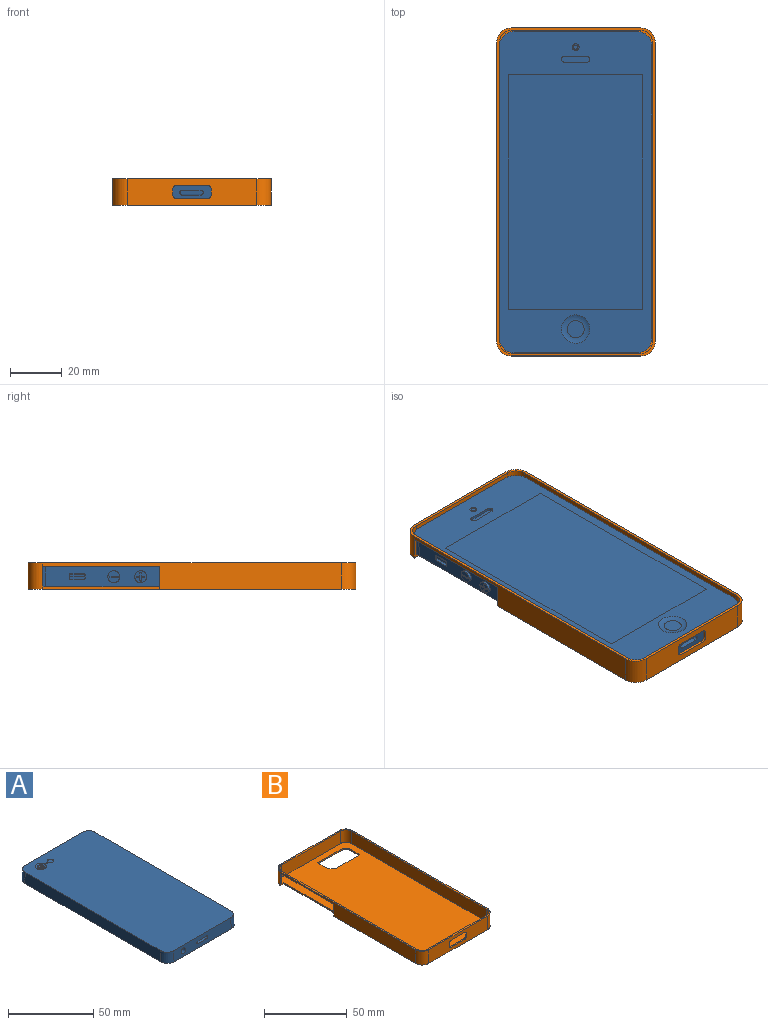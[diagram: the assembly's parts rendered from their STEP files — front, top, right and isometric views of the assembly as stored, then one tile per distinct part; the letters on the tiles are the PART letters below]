
ASSEMBLY  parts=2 mates=1
PART A: 118 faces, bbox 59.5x124.3x7.6 mm
  f0: plane 47.4x7.6mm, normal (0,1,0.05), area 338.2mm2, adj f6,f7,f9,f10,f109,f110,f111,f112
  f1: plane 6x2.52mm, normal (1,0,0.05), area 9.6mm2, adj f40,f41,f42,f43,f44,f45,f46,f47
  f2: cone r=5.6mm half-angle=3deg, axis (0,0,-1), area 64.6mm2, adj f3,f8,f9,f10
  f3: plane 47.4x7.6mm, normal (0,-1,0.05), area 334.5mm2, adj f2,f4,f9,f10,f29,f30,f31,f32
  f4: cone r=5.6mm half-angle=3deg, axis (0,0,-1), area 64.6mm2, adj f3,f5,f9,f10
  f5: plane 112.6x7.6mm, normal (1,0,0.05), area 808.8mm2, adj f4,f6,f9,f10,f40,f41,f42,f43
  f6: cone r=5.6mm half-angle=3deg, axis (0,0,-1), area 64.6mm2, adj f0,f5,f9,f10
  f7: cone r=5.6mm half-angle=3deg, axis (0,0,-1), area 64.6mm2, adj f0,f8,f9,f10
  f8: plane 112.6x7.6mm, normal (-1,0,0.05), area 856.9mm2, adj f2,f7,f9,f10
  f9: plane 123x57.8mm, normal (0,0,1), area 7041.8mm2, adj f0,f2,f3,f4,f5,f6,f7,f8
  f10: plane 123.8x58.6mm, normal (0,0,-1), area 2431.8mm2, adj f0,f2,f3,f4,f5,f6,f7,f8
  f11: plane 6.54x6.54mm, normal (0,0,-1), area 33.6mm2, adj f12
  f12: torus R=3.27mm, axis (0,0,1), area 62mm2, adj f10,f11
  f13: plane 90.39x0mm, normal (1,0,0), area 0mm2, adj f10,f17
  f14: plane 51.7x0mm, normal (0,-1,0), area 0mm2, adj f10,f17
  f15: plane 90.39x0mm, normal (-1,0,0), area 0mm2, adj f10,f17
  f16: plane 51.7x0mm, normal (0,1,0), area 0mm2, adj f10,f17
  f17: plane 90.39x51.7mm, normal (0,0,-1), area 4673.2mm2, adj f13,f14,f15,f16
  f18: cylinder r=1.1mm len=1.1mm, axis (0,0,-1), area 1.7mm2, adj f10,f19,f25,f26
  f19: plane 8.7x1mm, normal (0,1,0), area 8.7mm2, adj f10,f18,f20,f26
  f20: cylinder r=1.1mm len=1.1mm, axis (0,0,-1), area 1.7mm2, adj f10,f19,f21,f26
  f21: plane 1x0.1mm, normal (1,0,0), area 0.1mm2, adj f10,f20,f22,f26
  f22: cylinder r=1.1mm len=1.1mm, axis (0,0,-1), area 1.7mm2, adj f10,f21,f23,f26
  f23: plane 8.7x1mm, normal (0,-1,0), area 8.7mm2, adj f10,f22,f24,f26
  f24: cylinder r=1.1mm len=1.1mm, axis (0,0,-1), area 1.7mm2, adj f10,f23,f25,f26
  f25: plane 1x0.1mm, normal (-1,0,0), area 0.1mm2, adj f10,f18,f24,f26
  f26: plane 10.9x2.3mm, normal (0,0,-1), area 24mm2, adj f18,f19,f20,f21,f22,f23,f24,f25
  f27: plane 1.56x1.56mm, normal (0,0,-1), area 1.9mm2, adj f28
  f28: torus R=0.78mm, axis (0,0,1), area 3.6mm2, adj f10,f27
  f29: cylinder r=0.9mm len=5.04mm, axis (0,-1,0.05), area 7.1mm2, adj f3,f30,f36,f37
  f30: plane 7.25x4.99mm, normal (0,0.05,1), area 36.2mm2, adj f3,f29,f31,f37
  f31: cylinder r=0.9mm len=5.04mm, axis (0,-1,0.05), area 7.1mm2, adj f3,f30,f32,f37
  f32: plane 5x0.34mm, normal (-1,0,0), area 0.4mm2, adj f3,f31,f33,f37
  f33: cylinder r=0.9mm len=5.04mm, axis (0,-1,0.05), area 7.1mm2, adj f3,f32,f34,f37
  f34: plane 7.25x4.99mm, normal (0,-0.05,-1), area 36.3mm2, adj f3,f33,f35,f37
  f35: cylinder r=0.9mm len=5.04mm, axis (0,-1,0.05), area 7.1mm2, adj f3,f34,f36,f37
  f36: plane 5x0.34mm, normal (1,0,0), area 0.4mm2, adj f3,f29,f35,f37
  f37: plane 9.05x1.88mm, normal (0,-1,0.05), area 16.3mm2, adj f29,f30,f31,f32,f33,f34,f35,f36
  f38: cylinder r=1.78mm len=10.17mm, axis (0,-1,0.05), area 111.8mm2, adj f3,f39
  f39: plane 3.56x3.56mm, normal (0,-1,0.05), area 10mm2, adj f38
  f40: plane 5x1.5mm, normal (-0.05,0,1), area 7.5mm2, adj f1,f5,f41,f47
  f41: cylinder r=0.5mm len=1.52mm, axis (1,0,0.05), area 1.2mm2, adj f1,f5,f40,f42
  f42: plane 1.6x1.58mm, normal (0,-1,0), area 2.3mm2, adj f1,f5,f41,f43
  f43: cylinder r=0.5mm len=1.52mm, axis (1,0,0.05), area 1.2mm2, adj f1,f5,f42,f44
  f44: plane 5x1.5mm, normal (0.05,0,-1), area 7.5mm2, adj f1,f5,f43,f45
  f45: cylinder r=0.5mm len=1.52mm, axis (1,0,0.05), area 1.2mm2, adj f1,f5,f44,f46
  f46: plane 1.6x1.58mm, normal (0,1,0), area 2.3mm2, adj f1,f5,f45,f47
  f47: cylinder r=0.5mm len=1.52mm, axis (1,0,0.05), area 1.2mm2, adj f1,f5,f40,f46
  f48: cylinder r=2.3mm len=4.65mm, axis (-1,0,-0.05), area 14.5mm2, adj f5,f49
  f49: plane 4.6x4.59mm, normal (1,0,0.05), area 15.1mm2, adj f48,f61,f62,f63,f64,f65,f66,f67
  f50: cylinder r=2.3mm len=4.65mm, axis (-1,0,-0.05), area 14.5mm2, adj f5,f51
  f51: plane 4.6x4.59mm, normal (1,0,0.05), area 13.8mm2, adj f50,f70,f71,f72,f73,f74,f75,f76
  f52: cylinder r=0.4mm len=1.62mm, axis (-1,0,-0.05), area 1mm2, adj f1,f53,f59,f60
  f53: plane 5x1.6mm, normal (0.05,0,-1), area 8mm2, adj f1,f52,f54,f60
  f54: cylinder r=0.4mm len=1.62mm, axis (-1,0,-0.05), area 1mm2, adj f1,f53,f55,f60
  f55: plane 1.61x0.22mm, normal (0,1,0), area 0.2mm2, adj f1,f54,f56,f60
  f56: cylinder r=0.4mm len=1.62mm, axis (-1,0,-0.05), area 1mm2, adj f1,f55,f57,f60
  f57: plane 5x1.6mm, normal (-0.05,0,1), area 8mm2, adj f1,f56,f58,f60
  f58: cylinder r=0.4mm len=1.62mm, axis (-1,0,-0.05), area 1mm2, adj f1,f57,f59,f60
  f59: plane 1.61x0.22mm, normal (0,-1,0), area 0.2mm2, adj f1,f52,f58,f60
  f60: plane 5.8x0.94mm, normal (1,0,0.05), area 5.3mm2, adj f52,f53,f54,f55,f56,f57,f58,f59
  f61: cylinder r=0.2mm len=0.21mm, axis (1,0,0.05), area 0mm2, adj f49,f62,f68,f69
  f62: plane 3x0.1mm, normal (-0.05,0,1), area 0.3mm2, adj f49,f61,f63,f69
  f63: cylinder r=0.2mm len=0.21mm, axis (1,0,0.05), area 0mm2, adj f49,f62,f64,f69
  f64: plane 0.1x0.06mm, normal (0,-1,0), area 0mm2, adj f49,f63,f65,f69
  f65: cylinder r=0.2mm len=0.21mm, axis (1,0,0.05), area 0mm2, adj f49,f64,f66,f69
  f66: plane 3x0.1mm, normal (0.05,0,-1), area 0.3mm2, adj f49,f65,f67,f69
  f67: cylinder r=0.2mm len=0.21mm, axis (1,0,0.05), area 0mm2, adj f49,f66,f68,f69
  f68: plane 0.1x0.06mm, normal (0,1,0), area 0mm2, adj f49,f61,f67,f69
  f69: plane 3.4x0.45mm, normal (1,0,0.05), area 1.5mm2, adj f61,f62,f63,f64,f65,f66,f67,f68
  f70: plane 1.27x0.1mm, normal (-0.05,0,1), area 0.1mm2, adj f51,f71,f89,f90
  f71: plane 1.28x0.17mm, normal (0,1,0), area 0.1mm2, adj f51,f70,f72,f90
  f72: cylinder r=0.2mm len=0.21mm, axis (1,0,0.05), area 0mm2, adj f51,f71,f73,f90
  f73: plane 0.1x0.05mm, normal (-0.05,0,1), area 0mm2, adj f51,f72,f74,f90
  f74: cylinder r=0.2mm len=0.21mm, axis (1,0,0.05), area 0mm2, adj f51,f73,f75,f90
  f75: plane 1.28x0.17mm, normal (0,-1,0), area 0.1mm2, adj f51,f74,f76,f90
  f76: plane 1.27x0.1mm, normal (-0.05,0,1), area 0.1mm2, adj f51,f75,f77,f90
  f77: cylinder r=0.2mm len=0.21mm, axis (1,0,0.05), area 0mm2, adj f51,f76,f78,f90
  f78: plane 0.1x0.06mm, normal (0,-1,0), area 0mm2, adj f51,f77,f79,f90
  f79: cylinder r=0.2mm len=0.21mm, axis (1,0,0.05), area 0mm2, adj f51,f78,f80,f90
  f80: plane 1.27x0.1mm, normal (0.05,0,-1), area 0.1mm2, adj f51,f79,f81,f90
  f81: plane 1.28x0.17mm, normal (0,-1,0), area 0.1mm2, adj f51,f80,f82,f90
  f82: cylinder r=0.2mm len=0.21mm, axis (1,0,0.05), area 0mm2, adj f51,f81,f83,f90
  f83: plane 0.1x0.05mm, normal (0.05,0,-1), area 0mm2, adj f51,f82,f84,f90
  f84: cylinder r=0.2mm len=0.21mm, axis (1,0,0.05), area 0mm2, adj f51,f83,f85,f90
  f85: plane 1.28x0.17mm, normal (0,1,0), area 0.1mm2, adj f51,f84,f86,f90
  f86: plane 1.27x0.1mm, normal (0.05,0,-1), area 0.1mm2, adj f51,f85,f87,f90
  f87: cylinder r=0.2mm len=0.21mm, axis (1,0,0.05), area 0mm2, adj f51,f86,f88,f90
  f88: plane 0.1x0.06mm, normal (0,1,0), area 0mm2, adj f51,f87,f89,f90
  f89: cylinder r=0.2mm len=0.21mm, axis (1,0,0.05), area 0mm2, adj f51,f70,f88,f90
  f90: plane 3.4x3.4mm, normal (1,0,0.05), area 2.8mm2, adj f70,f71,f72,f73,f74,f75,f76,f77
  f91: cylinder r=0.49mm len=0.86mm, axis (0,0,1), area 0.7mm2, adj f9,f92,f98,f99
  f92: plane 0.86x0.67mm, normal (0,1,0), area 0.6mm2, adj f9,f91,f93,f99
  f93: cylinder r=0.49mm len=0.86mm, axis (0,0,1), area 0.7mm2, adj f9,f92,f94,f99
  f94: plane 0.86x0.04mm, normal (-1,0,0), area 0mm2, adj f9,f93,f95,f99
  f95: cylinder r=0.49mm len=0.86mm, axis (0,0,1), area 0.7mm2, adj f9,f94,f96,f99
  f96: plane 0.86x0.67mm, normal (0,-1,0), area 0.6mm2, adj f9,f95,f97,f99
  f97: cylinder r=0.49mm len=0.86mm, axis (0,0,1), area 0.7mm2, adj f9,f96,f98,f99
  f98: plane 0.86x0.04mm, normal (1,0,0), area 0mm2, adj f9,f91,f97,f99
  f99: plane 1.65x1.02mm, normal (0,0,1), area 1.5mm2, adj f91,f92,f93,f94,f95,f96,f97,f98
  f100: cylinder r=1.85mm len=3.7mm, axis (0,0,1), area 4mm2, adj f9,f101
  f101: plane 3.7x3.7mm, normal (0,0,1), area 10.8mm2, adj f100
  f102: torus R=1.42mm, axis (0,0,-1), area 27.2mm2, adj f9,f105
  f103: cylinder r=2.12mm len=4.23mm, axis (0,0,1), area 6.6mm2, adj f104,f105
  f104: plane 4.23x4.23mm, normal (0,0,1), area 12.7mm2, adj f103,f106
  f105: plane 4.23x4.23mm, normal (0,0,-1), area 7.7mm2, adj f102,f103
  f106: cylinder r=0.65mm len=1.3mm, axis (0,0,-1), area 0.4mm2, adj f104,f108
  f107: plane 1.1x1.1mm, normal (0,0,1), area 1mm2, adj f108
  f108: torus R=0.55mm, axis (0,0,1), area 0.6mm2, adj f106,f107
  f109: cylinder r=1mm len=1.03mm, axis (0,-1,-0.05), area 1.1mm2, adj f0,f110,f116,f117
  f110: plane 7.5x0.67mm, normal (0,0.05,-1), area 5mm2, adj f0,f109,f111,f117
  f111: cylinder r=1mm len=1.03mm, axis (0,-1,-0.05), area 1.1mm2, adj f0,f110,f112,f117
  f112: plane 0.69x0.49mm, normal (-1,0,0), area 0.3mm2, adj f0,f111,f113,f117
  f113: cylinder r=1mm len=1.03mm, axis (0,-1,-0.05), area 1.1mm2, adj f0,f112,f114,f117
  f114: plane 7.5x0.67mm, normal (0,-0.05,1), area 5mm2, adj f0,f113,f115,f117
  f115: cylinder r=1mm len=1.03mm, axis (0,-1,-0.05), area 1.1mm2, adj f0,f114,f116,f117
  f116: plane 0.69x0.49mm, normal (1,0,0), area 0.3mm2, adj f0,f109,f115,f117
  f117: plane 9.5x2.46mm, normal (0,1,0.05), area 22.5mm2, adj f109,f110,f111,f112,f113,f114,f115,f116
PART B: 38 faces, bbox 61.1x126.3x10.1 mm
  f0: plane 115.1x10.1mm, normal (-1,0,0), area 765mm2, adj f1,f7,f8,f9,f26,f27
  f1: cylinder r=5.6mm len=10.1mm, axis (0,0,-1), area 88.8mm2, adj f0,f2,f8,f9
  f2: plane 49.9x10.1mm, normal (0,-1,0), area 429.1mm2, adj f1,f3,f8,f9,f30,f31,f32,f33
  f3: cylinder r=5.6mm len=10.1mm, axis (0,0,-1), area 88.8mm2, adj f2,f4,f8,f9
  f4: plane 115.1x10.1mm, normal (1,0,0), area 1162.5mm2, adj f3,f5,f8,f9
  f5: cylinder r=5.6mm len=10.1mm, axis (0,0,-1), area 88.8mm2, adj f4,f6,f8,f9
  f6: plane 49.9x10.1mm, normal (0,1,0), area 504mm2, adj f5,f7,f8,f9
  f7: cylinder r=5.6mm len=10.1mm, axis (0,0,-1), area 88.8mm2, adj f0,f6,f8,f9,f28
  f8: plane 126.3x61.1mm, normal (0,0,1), area 362mm2, adj f0,f1,f2,f3,f4,f5,f6,f7
  f9: plane 126.3x61.1mm, normal (0,0,-1), area 7299.4mm2, adj f0,f1,f2,f3,f4,f5,f6,f7
  f10: cylinder r=4.6mm len=9.1mm, axis (0,0,-1), area 65.8mm2, adj f8,f11,f17,f18
  f11: plane 49.9x9.1mm, normal (0,1,0), area 379.2mm2, adj f8,f10,f12,f18,f30,f31,f32,f33
  f12: cylinder r=4.6mm len=9.1mm, axis (0,0,-1), area 65.8mm2, adj f8,f11,f13,f18
  f13: plane 115.1x9.1mm, normal (-1,0,0), area 1047.4mm2, adj f8,f12,f14,f18
  f14: cylinder r=4.6mm len=9.1mm, axis (0,0,-1), area 65.8mm2, adj f8,f13,f15,f18
  f15: plane 49.9x9.1mm, normal (0,-1,0), area 454.1mm2, adj f8,f14,f16,f18
  f16: cylinder r=4.6mm len=9.1mm, axis (0,0,-1), area 65.8mm2, adj f8,f15,f17,f18,f28
  f17: plane 115.1x9.1mm, normal (1,0,0), area 695.1mm2, adj f8,f10,f16,f18,f26,f27
  f18: plane 124.3x59.1mm, normal (0,0,1), area 6982.5mm2, adj f10,f11,f12,f13,f14,f15,f16,f17
  f19: plane 7.54x1mm, normal (-1,0,0), area 7.5mm2, adj f9,f18,f20,f25
  f20: cylinder r=0.4mm len=1mm, axis (0,0,-1), area 0.6mm2, adj f9,f18,f19,f21
  f21: plane 18.35x1mm, normal (0,1,0), area 18.4mm2, adj f9,f18,f20,f22
  f22: cylinder r=5.3mm len=5.3mm, axis (0,0,-1), area 8.3mm2, adj f9,f18,f21,f23
  f23: plane 6.64x1mm, normal (1,0,0), area 6.6mm2, adj f9,f18,f22,f24
  f24: plane 20.05x1mm, normal (0,-1,0), area 20.1mm2, adj f9,f18,f23,f25
  f25: cylinder r=4mm len=4mm, axis (0,0,-1), area 6.3mm2, adj f9,f18,f19,f24
  f26: plane 8.8x2.5mm, normal (0,1,0), area 10.3mm2, adj f0,f9,f17,f18,f27,f29
  f27: plane 45.17x1mm, normal (0,0,-1), area 45.2mm2, adj f0,f17,f26,f28
  f28: plane 8.8x2.5mm, normal (0,-1,0), area 10.3mm2, adj f7,f9,f16,f18,f27,f29
  f29: plane 45.17x1mm, normal (-1,0,0), area 45.2mm2, adj f9,f18,f26,f28
  f30: cylinder r=1.75mm len=1.75mm, axis (0,-1,0), area 2.7mm2, adj f2,f11,f31,f37
  f31: plane 11.48x1mm, normal (0,0,1), area 11.5mm2, adj f2,f11,f30,f32
  f32: cylinder r=1.75mm len=1.75mm, axis (0,-1,0), area 2.7mm2, adj f2,f11,f31,f33
  f33: plane 1.68x1mm, normal (-1,0,0), area 1.7mm2, adj f2,f11,f32,f34
  f34: cylinder r=1.75mm len=1.75mm, axis (0,-1,0), area 2.7mm2, adj f2,f11,f33,f35
  f35: plane 11.48x1mm, normal (0,0,-1), area 11.5mm2, adj f2,f11,f34,f36
  f36: cylinder r=1.75mm len=1.75mm, axis (0,-1,0), area 2.7mm2, adj f2,f11,f35,f37
  f37: plane 1.68x1mm, normal (1,0,0), area 1.7mm2, adj f2,f11,f30,f36
PLACE A rot(axis=(0,1,0),180deg) t=(-2.05,-5,-1.23)mm
PLACE B t=(-1.92,-4.95,-9.83)mm
MATE fastened A.f9 <-> B.f18  axis (0,0,-1) through (-2.16,-5.34,-8.83)mm
